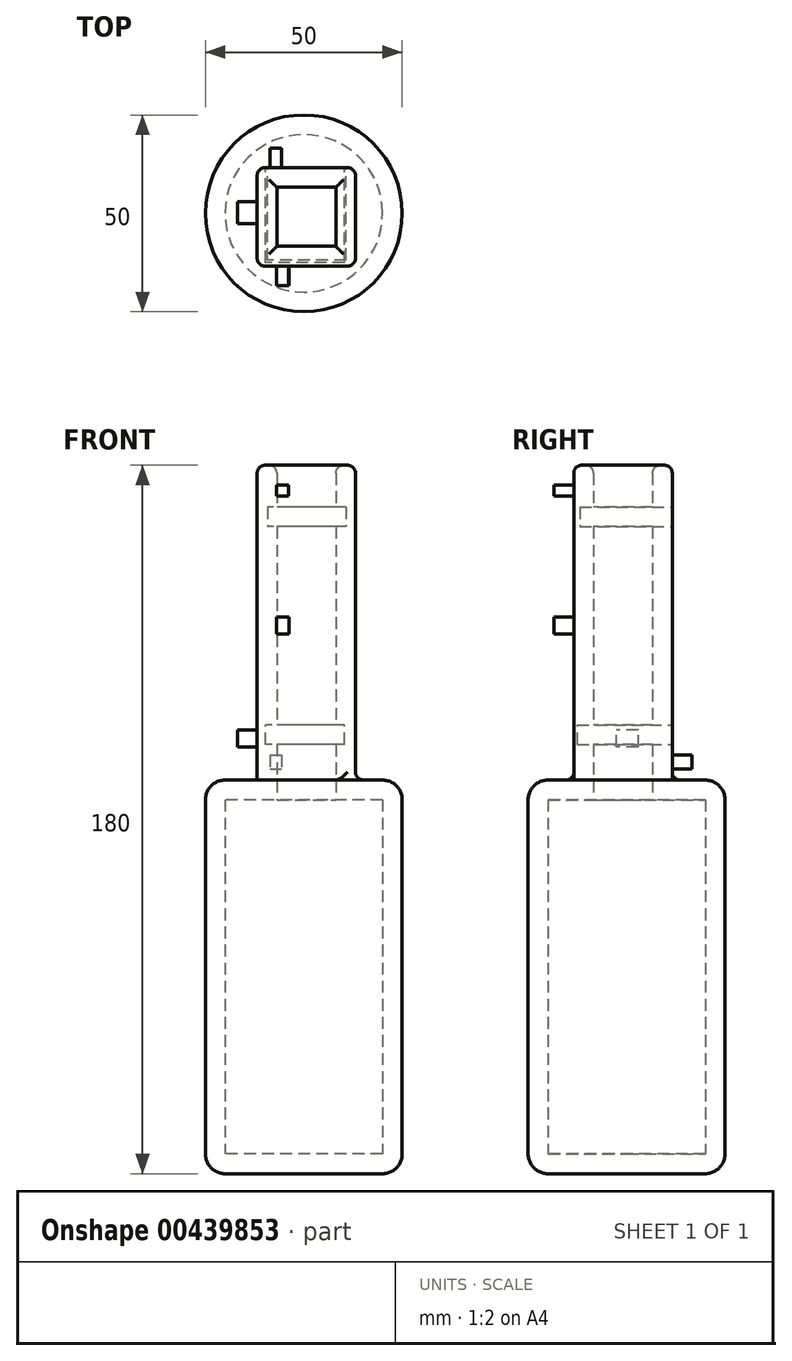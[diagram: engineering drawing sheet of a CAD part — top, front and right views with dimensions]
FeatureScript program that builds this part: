
annotation { "Feature Type Name" : "Feature", "Feature Type Description" : "" }
export const myFeature = defineFeature(function(context is Context, id is Id, definition is map)
    precondition{}
    {
        {
            var Q0;
            Q0=qCreatedBy(makeId("Top.planeOp"),FACE);
            var sketch = newSketch(context, id + "F0", { "sketchPlane" : qUnion([Q0])});
            skCircle(sketch, "E0", {"center": v(-20.56, 0) * mm, "radius": 25 * mm});
            skSolve(sketch);
        }
        {
            var Q0;
            Q0 = qSketchRegion(id + "F0", true);
            extrude(context, id + "F1", {"entities" : qUnion([Q0]), "depth" : 100 * mm});
        }
        {
            var Q0;
            Q0=makeQuery(id+"F1.opExtrude","CAP_FACE",FACE,{"disambiguationData":[OSD([sQuery(id+"F0.wireOp",EDGE,"E0")])],"isStart":false});
            var sketch = newSketch(context, id + "F2", { "sketchPlane" : qUnion([Q0])});
            skLineSegment(sketch, "E1.bottom", {"start": v(-32.42, -13.4) * mm, "end": v(-7.42, -13.4) * mm});
            skLineSegment(sketch, "E1.top", {"start": v(-32.42, 11.6) * mm, "end": v(-7.42, 11.6) * mm});
            skLineSegment(sketch, "E1.left", {"start": v(-32.42, -13.4) * mm, "end": v(-32.42, 11.6) * mm});
            skLineSegment(sketch, "E1.right", {"start": v(-7.42, -13.4) * mm, "end": v(-7.42, 11.6) * mm});
            skSolve(sketch);
        }
        {
            var Q0;
            Q0 = qSketchRegion(id + "F2", true);
            extrude(context, id + "F3", {"entities" : qUnion([Q0]), "operationType" : NewBodyOperationType.ADD, "depth" : 80 * mm});
        }
        {
            var Q0;
            Q0=makeQuery(id+"F3.opExtrude","SWEPT_FACE",FACE,{"disambiguationData":[OSD([sQuery(id+"F2.wireOp",EDGE,"E1.top")])]});
            var sketch = newSketch(context, id + "F4", { "sketchPlane" : qUnion([Q0])});
            skLineSegment(sketch, "E2.bottom", {"start": v(9.8, 169.38) * mm, "end": v(29.8, 169.38) * mm});
            skLineSegment(sketch, "E2.top", {"start": v(9.8, 164.38) * mm, "end": v(29.8, 164.38) * mm});
            skLineSegment(sketch, "E2.left", {"start": v(9.8, 169.38) * mm, "end": v(9.8, 164.38) * mm});
            skLineSegment(sketch, "E2.right", {"start": v(29.8, 169.38) * mm, "end": v(29.8, 164.38) * mm});
            skSolve(sketch);
        }
        {
            var Q0;
            Q0=makeQuery(id+"F4.imprint","IMPRINT",FACE,{"disambiguationData":[TD([[makeQuery(id+"F4.imprint","IMPRINT",EDGE,{"derivedFrom":sQuery(id+"F4.wireOp",EDGE,"E2.bottom")}),-1.0]])]});
            extrude(context, id + "F5", {"entities" : qUnion([Q0]), "operationType" : NewBodyOperationType.REMOVE, "oppositeDirection" : true, "depth" : 23.5 * mm});
        }
        {
            var Q0;
            Q0=makeQuery(id+"F3.opExtrude","SWEPT_FACE",FACE,{"disambiguationData":[OSD([sQuery(id+"F2.wireOp",EDGE,"E1.top")])]});
            var sketch = newSketch(context, id + "F6", { "sketchPlane" : qUnion([Q0])});
            skLineSegment(sketch, "E3.bottom", {"start": v(10.23, 109.05) * mm, "end": v(30.23, 109.05) * mm});
            skLineSegment(sketch, "E3.top", {"start": v(10.23, 114.05) * mm, "end": v(30.23, 114.05) * mm});
            skLineSegment(sketch, "E3.left", {"start": v(10.23, 109.05) * mm, "end": v(10.23, 114.05) * mm});
            skLineSegment(sketch, "E3.right", {"start": v(30.23, 109.05) * mm, "end": v(30.23, 114.05) * mm});
            skSolve(sketch);
        }
        {
            var Q0;
            Q0=makeQuery(id+"F6.imprint","IMPRINT",FACE,{"disambiguationData":[TD([[makeQuery(id+"F6.imprint","IMPRINT",EDGE,{"derivedFrom":sQuery(id+"F6.wireOp",EDGE,"E3.bottom")}),1.0]])]});
            extrude(context, id + "F7", {"entities" : qUnion([Q0]), "operationType" : NewBodyOperationType.REMOVE, "oppositeDirection" : true, "depth" : 24.1 * mm});
        }
        {
            var Q0;
            Q0=makeQuery(id+"F3.opExtrude","CAP_FACE",FACE,{"disambiguationData":[OSD([sQuery(id+"F2.wireOp",EDGE,"E1.bottom"),sQuery(id+"F2.wireOp",EDGE,"E1.top"),sQuery(id+"F2.wireOp",EDGE,"E1.left"),sQuery(id+"F2.wireOp",EDGE,"E1.right")])],"isStart":false});
            shell(context, id + "F8", {"entities" : qUnion([Q0]), "thickness" : 5 * mm});
        }
        {
            var Q0;
            Q0=makeQuery(id+"F8.opShell","OFFSET_FACE",FACE,{"disambiguationData":[OSD([sQuery(id+"F4.wireOp",EDGE,"E2.bottom")])]});
            extrude(context, id + "F9", {"entities" : qUnion([Q0]), "operationType" : NewBodyOperationType.REMOVE, "oppositeDirection" : true, "depth" : 86 * mm});
        }
        {
            var Q0;
            Q0=makeQuery(id+"F3.opExtrude","SWEPT_FACE",FACE,{"disambiguationData":[OSD([sQuery(id+"F2.wireOp",EDGE,"E1.bottom")])]});
            var sketch = newSketch(context, id + "F10", { "sketchPlane" : qUnion([Q0])});
            skLineSegment(sketch, "E4.bottom", {"start": v(-24.5, 175.01) * mm, "end": v(-27.52, 175.01) * mm});
            skLineSegment(sketch, "E4.top", {"start": v(-24.5, 172.2) * mm, "end": v(-27.52, 172.2) * mm});
            skLineSegment(sketch, "E4.left", {"start": v(-24.5, 175.01) * mm, "end": v(-24.5, 172.2) * mm});
            skLineSegment(sketch, "E4.right", {"start": v(-27.52, 175.01) * mm, "end": v(-27.52, 172.2) * mm});
            skLineSegment(sketch, "E5.bottom", {"start": v(-27.52, 141.37) * mm, "end": v(-24.32, 141.37) * mm});
            skLineSegment(sketch, "E5.top", {"start": v(-27.52, 137.06) * mm, "end": v(-24.32, 137.06) * mm});
            skLineSegment(sketch, "E5.left", {"start": v(-27.52, 141.37) * mm, "end": v(-27.52, 137.06) * mm});
            skLineSegment(sketch, "E5.right", {"start": v(-24.32, 141.37) * mm, "end": v(-24.32, 137.06) * mm});
            skSolve(sketch);
        }
        {
            var Q0;
            Q0=makeQuery(id+"F10.imprint","IMPRINT",FACE,{"disambiguationData":[TD([[makeQuery(id+"F10.imprint","IMPRINT",EDGE,{"derivedFrom":sQuery(id+"F10.wireOp",EDGE,"E4.bottom")}),1.0]])]});
            var Q1;
            Q1=makeQuery(id+"F10.imprint","IMPRINT",FACE,{"disambiguationData":[TD([[makeQuery(id+"F10.imprint","IMPRINT",EDGE,{"derivedFrom":sQuery(id+"F10.wireOp",EDGE,"E5.bottom")}),-1.0]])]});
            extrude(context, id + "F11", {"entities" : qUnion([Q0, Q1]), "operationType" : NewBodyOperationType.ADD, "depth" : 5 * mm});
        }
        {
            var Q0;
            Q0=makeQuery(id+"F3.opExtrude","SWEPT_FACE",FACE,{"disambiguationData":[OSD([sQuery(id+"F2.wireOp",EDGE,"E1.left")])]});
            var sketch = newSketch(context, id + "F12", { "sketchPlane" : qUnion([Q0])});
            skLineSegment(sketch, "E6.bottom", {"start": v(-2.97, 108.45) * mm, "end": v(2.61, 108.45) * mm});
            skLineSegment(sketch, "E6.top", {"start": v(-2.97, 112.7) * mm, "end": v(2.61, 112.7) * mm});
            skLineSegment(sketch, "E6.left", {"start": v(-2.97, 108.45) * mm, "end": v(-2.97, 112.7) * mm});
            skLineSegment(sketch, "E6.right", {"start": v(2.61, 108.45) * mm, "end": v(2.61, 112.7) * mm});
            skSolve(sketch);
        }
        {
            var Q0;
            Q0 = qSketchRegion(id + "F12", true);
            extrude(context, id + "F13", {"entities" : qUnion([Q0]), "operationType" : NewBodyOperationType.ADD, "depth" : 5 * mm});
        }
        {
            var Q0;
            Q0=makeQuery(id+"F3.opExtrude","SWEPT_FACE",FACE,{"disambiguationData":[OSD([sQuery(id+"F2.wireOp",EDGE,"E1.top")])]});
            var sketch = newSketch(context, id + "F14", { "sketchPlane" : qUnion([Q0])});
            skLineSegment(sketch, "E7.bottom", {"start": v(29.09, 106.34) * mm, "end": v(26.2, 106.34) * mm});
            skLineSegment(sketch, "E7.top", {"start": v(29.09, 102.77) * mm, "end": v(26.2, 102.77) * mm});
            skLineSegment(sketch, "E7.left", {"start": v(29.09, 106.34) * mm, "end": v(29.09, 102.77) * mm});
            skLineSegment(sketch, "E7.right", {"start": v(26.2, 106.34) * mm, "end": v(26.2, 102.77) * mm});
            skSolve(sketch);
        }
        {
            var Q0;
            Q0 = qSketchRegion(id + "F14", true);
            extrude(context, id + "F15", {"entities" : qUnion([Q0]), "operationType" : NewBodyOperationType.ADD, "depth" : 5 * mm});
        }
        {
            var Q0;
            Q0=makeQuery(id+"F1.opExtrude","CAP_FACE",FACE,{"disambiguationData":[OSD([sQuery(id+"F0.wireOp",EDGE,"E0")])],"isStart":true});
            var Q1;
            Q1=makeQuery(id+"F1.opExtrude","CAP_EDGE",EDGE,{"disambiguationData":[OSD([sQuery(id+"F0.wireOp",EDGE,"E0")])],"isStart":false});
            fillet(context, id + "F16", {"entities" : qUnion([Q0, Q1]), "radius" : 5 * mm, "tangentPropagation" : true, "allowEdgeOverflow" : false});
        }
        {
            var Q0;
            Q0=makeQuery(id+"F3.opExtrude","CAP_FACE",FACE,{"disambiguationData":[OSD([sQuery(id+"F2.wireOp",EDGE,"E1.bottom"),sQuery(id+"F2.wireOp",EDGE,"E1.top"),sQuery(id+"F2.wireOp",EDGE,"E1.left"),sQuery(id+"F2.wireOp",EDGE,"E1.right")])],"isStart":false});
            fillet(context, id + "F17", {"entities" : qUnion([Q0]), "radius" : 2 * mm, "tangentPropagation" : true, "allowEdgeOverflow" : false});
        }
        {
            var Q0;
            Q0=makeQuery(id+"F3.opExtrude","SWEPT_FACE",FACE,{"disambiguationData":[OSD([sQuery(id+"F2.wireOp",EDGE,"E1.right")])]});
            var Q1;
            Q1=makeQuery(id+"F3.opExtrude","SWEPT_EDGE",EDGE,{"disambiguationData":[OSD([sQuery(id+"F2.wireOp",EDGE,"E1.bottom"),sQuery(id+"F2.wireOp",EDGE,"E1.left")])]});
            var Q2;
            Q2=makeQuery(id+"F3.opExtrude","SWEPT_EDGE",EDGE,{"disambiguationData":[OSD([sQuery(id+"F2.wireOp",EDGE,"E1.top"),sQuery(id+"F2.wireOp",EDGE,"E1.left")])]});
            fillet(context, id + "F18", {"entities" : qUnion([Q0, Q1, Q2]), "radius" : 2 * mm, "tangentPropagation" : true, "allowEdgeOverflow" : false});
        }
    });
